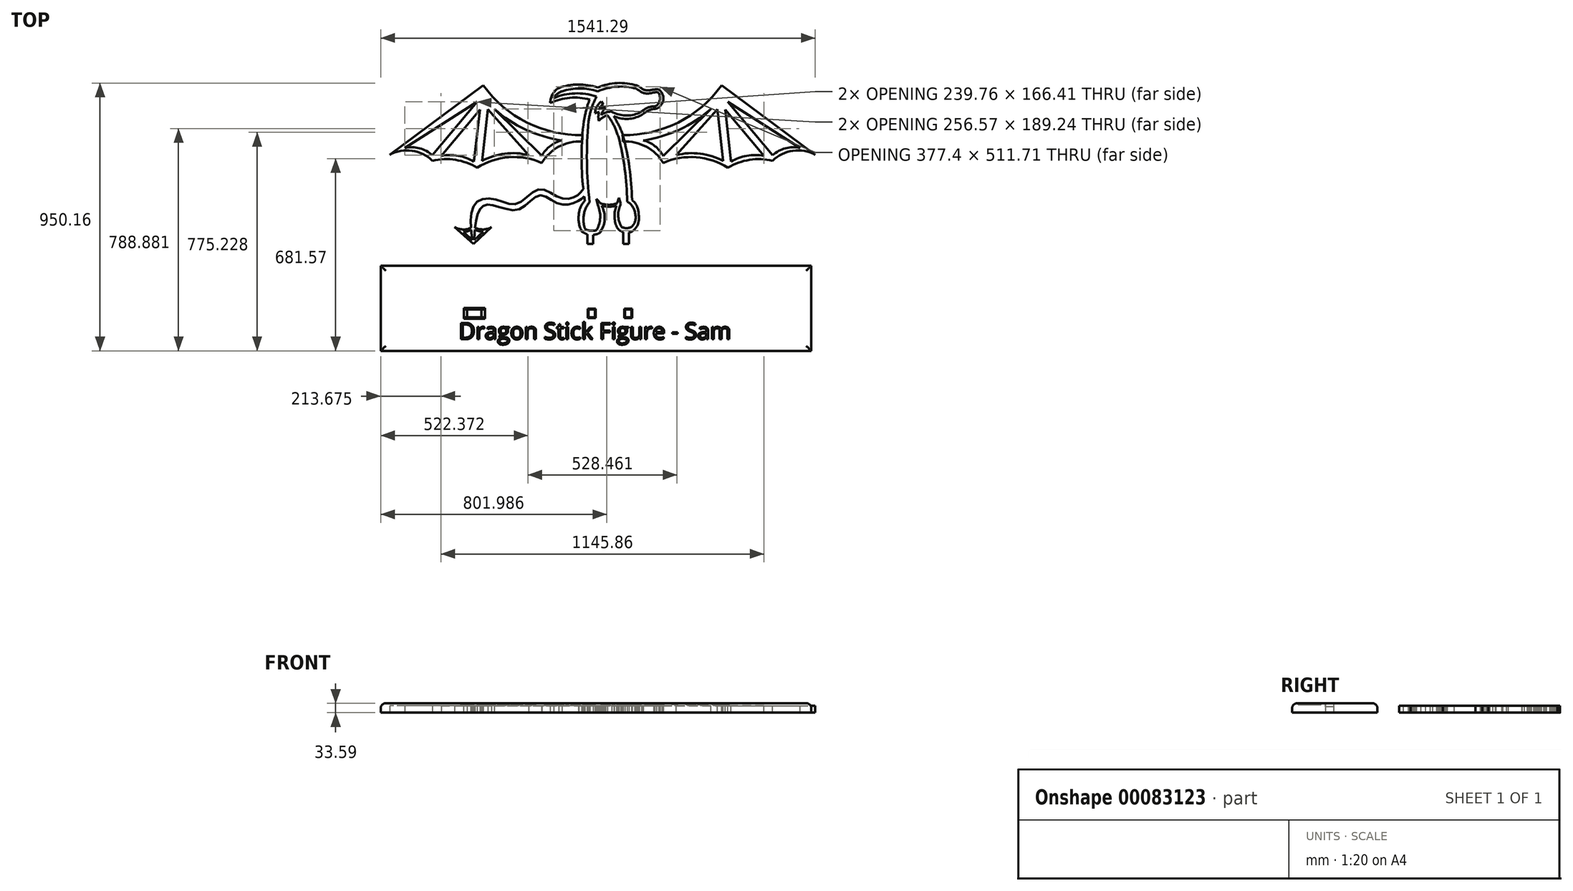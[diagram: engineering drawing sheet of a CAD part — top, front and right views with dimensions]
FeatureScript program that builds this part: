
annotation { "Feature Type Name" : "Feature", "Feature Type Description" : "" }
export const myFeature = defineFeature(function(context is Context, id is Id, definition is map)
    precondition{}
    {
        {
            var Q0;
            Q0=qCreatedBy(makeId("Top.planeOp"),FACE);
            var sketch = newSketch(context, id + "F0", { "sketchPlane" : qUnion([Q0])});
            skArc(sketch, "E0", {"start": v(-484.43, 280.49) * mm, "mid": v(-553.48, 287.44) * mm, "end": v(-620.94, 271.12) * mm});
            skFitSpline(sketch, "E1", {"points": [v(-484.43, 280.49) * mm, v(-460.99, 265.97) * mm, v(-442.45, 263.54) * mm, v(-427.16, 265.56) * mm, v(-405.15, 265.8) * mm], "startDerivative": vector(138.37, -75.5) * mm, "endDerivative": vector(39.99, -52.16) * mm});
            skArc(sketch, "E2", {"start": v(-412.1, 219.74) * mm, "mid": v(-400.2, 241.5) * mm, "end": v(-405.15, 265.8) * mm});
            skArc(sketch, "E3", {"start": v(-422.32, 217.88) * mm, "mid": v(-445.34, 212.23) * mm, "end": v(-465.2, 199.3) * mm});
            skFitSpline(sketch, "E4", {"points": [v(-422.32, 217.88) * mm, v(-417.9, 217.88) * mm, v(-412.1, 219.74) * mm], "startDerivative": vector(9.34, -0.8) * mm, "endDerivative": vector(11.04, 4.36) * mm});
            skArc(sketch, "E5", {"start": v(-571.52, 199) * mm, "mid": v(-522.88, 185.43) * mm, "end": v(-473.31, 195.06) * mm});
            skFitSpline(sketch, "E6", {"points": [v(-473.31, 195.06) * mm, v(-468.57, 197.4) * mm, v(-465.2, 199.3) * mm], "startDerivative": vector(9.2, 4.4) * mm, "endDerivative": vector(6.96, 4.05) * mm});
            skArc(sketch, "E7", {"start": v(-620.94, 271.12) * mm, "mid": v(-684.3, 280.9) * mm, "end": v(-747.67, 271.1) * mm});
            skArc(sketch, "E8", {"start": v(-621.17, 284.55) * mm, "mid": v(-690.53, 295.4) * mm, "end": v(-759.58, 282.78) * mm});
            skArc(sketch, "E9", {"start": v(-481.37, 291.76) * mm, "mid": v(-551.9, 300.36) * mm, "end": v(-621.17, 284.55) * mm});
            skFitSpline(sketch, "E10", {"points": [v(-481.37, 291.76) * mm, v(-459.76, 277.82) * mm, v(-442.69, 274.68) * mm, v(-425.28, 276.74) * mm, v(-404.78, 277.02) * mm], "startDerivative": vector(140.51, -71.44) * mm, "endDerivative": vector(88.36, -26.77) * mm});
            skArc(sketch, "E11", {"start": v(-399.61, 218.82) * mm, "mid": v(-388.09, 240.85) * mm, "end": v(-393.55, 265.1) * mm});
            skFitSpline(sketch, "E12", {"points": [v(-404.78, 277.02) * mm, v(-400.06, 273.87) * mm, v(-395.78, 269.14) * mm, v(-393.55, 265.1) * mm], "startDerivative": vector(12.2, -10.5) * mm, "endDerivative": vector(5.8, -13.5) * mm});
            skArc(sketch, "E13", {"start": v(-418.36, 208.78) * mm, "mid": v(-440.62, 203.04) * mm, "end": v(-459.86, 190.48) * mm});
            skFitSpline(sketch, "E14", {"points": [v(-418.36, 208.78) * mm, v(-413.9, 209.67) * mm, v(-409.93, 210.81) * mm, v(-405.82, 212.87) * mm, v(-402.08, 215.77) * mm, v(-399.61, 218.82) * mm], "startDerivative": vector(19.06, 3.38) * mm, "endDerivative": vector(13.35, 14.43) * mm});
            skArc(sketch, "E15", {"start": v(-571.39, 187.02) * mm, "mid": v(-522.75, 173.44) * mm, "end": v(-473.18, 183.07) * mm});
            skFitSpline(sketch, "E16", {"points": [v(-473.18, 183.07) * mm, v(-468.57, 185.12) * mm, v(-464.55, 187.8) * mm, v(-459.86, 190.48) * mm], "startDerivative": vector(12.57, 6.02) * mm, "endDerivative": vector(11.63, 6.29) * mm});
            skArc(sketch, "E17", {"start": v(-571.52, 199) * mm, "mid": v(-590.86, 196.58) * mm, "end": v(-608, 187.3) * mm});
            skArc(sketch, "E18", {"start": v(-592.56, 213.03) * mm, "mid": v(-602.14, 201.29) * mm, "end": v(-608, 187.3) * mm});
            skArc(sketch, "E19", {"start": v(-592.56, 213.03) * mm, "mid": v(-604.54, 212.08) * mm, "end": v(-616, 208.46) * mm});
            skArc(sketch, "E20", {"start": v(-601.14, 225.6) * mm, "mid": v(-609.5, 217.84) * mm, "end": v(-616, 208.46) * mm});
            skArc(sketch, "E21", {"start": v(-571.39, 187.02) * mm, "mid": v(-596.73, 182.14) * mm, "end": v(-616.75, 165.84) * mm});
            skArc(sketch, "E22", {"start": v(-616, 197.02) * mm, "mid": v(-618.73, 181.49) * mm, "end": v(-616.75, 165.84) * mm});
            skArc(sketch, "E23", {"start": v(-616, 197.02) * mm, "mid": v(-623.27, 195.8) * mm, "end": v(-630.3, 193.6) * mm});
            skArc(sketch, "E24", {"start": v(-608, 234.75) * mm, "mid": v(-623.95, 216.78) * mm, "end": v(-630.3, 193.6) * mm});
            skLineSegment(sketch, "E25", {"start": v(-608, 234.75) * mm, "end": v(-601.14, 225.6) * mm});
            skArc(sketch, "E26", {"start": v(-747.67, 271.1) * mm, "mid": v(-764.57, 261.68) * mm, "end": v(-777.2, 247.01) * mm});
            skArc(sketch, "E27", {"start": v(-626.3, 252.48) * mm, "mid": v(-702.26, 263.77) * mm, "end": v(-777.2, 247.01) * mm});
            skArc(sketch, "E28", {"start": v(-648.73, 242.02) * mm, "mid": v(-720.12, 248.02) * mm, "end": v(-789.38, 229.68) * mm});
            skArc(sketch, "E29", {"start": v(-759.58, 282.78) * mm, "mid": v(-781.46, 260.15) * mm, "end": v(-789.38, 229.68) * mm});
            skFitSpline(sketch, "E30", {"points": [v(-626.3, 252.48) * mm, v(-637.17, 226.96) * mm, v(-647.34, 194.9) * mm, v(-653.4, 165.01) * mm], "startDerivative": vector(-23.44, -90.04) * mm, "endDerivative": vector(-15.76, -95.9) * mm});
            skArc(sketch, "E31", {"start": v(-669.93, 166.15) * mm, "mid": v(-678.05, 24.8) * mm, "end": v(-666.54, -116.32) * mm});
            skFitSpline(sketch, "E32", {"points": [v(-669.93, 166.15) * mm, v(-664.3, 192.64) * mm, v(-654.82, 227.81) * mm, v(-648.73, 242.02) * mm], "startDerivative": vector(12.93, 74.9) * mm, "endDerivative": vector(30.43, 52.72) * mm});
            skArc(sketch, "E33", {"start": v(-653.4, 165.01) * mm, "mid": v(-659.24, 21.16) * mm, "end": v(-649.6, -122.5) * mm});
            skArc(sketch, "E34", {"start": v(-670.97, -177.12) * mm, "mid": v(-670.63, -196.15) * mm, "end": v(-666.82, -214.8) * mm});
            skArc(sketch, "E35", {"start": v(-687.44, -160.73) * mm, "mid": v(-687.67, -194.27) * mm, "end": v(-677.18, -226.13) * mm});
            skArc(sketch, "E36", {"start": v(-624.6, -220.87) * mm, "mid": v(-612.15, -177.08) * mm, "end": v(-620.85, -132.38) * mm});
            skArc(sketch, "E37", {"start": v(-677.18, -226.13) * mm, "mid": v(-646.07, -238.08) * mm, "end": v(-613.5, -231.05) * mm});
            skArc(sketch, "E38", {"start": v(-613.5, -231.05) * mm, "mid": v(-596.6, -168.62) * mm, "end": v(-625.32, -110.68) * mm});
            skArc(sketch, "E39", {"start": v(-666.54, -116.32) * mm, "mid": v(-680.3, -136.97) * mm, "end": v(-687.44, -160.73) * mm});
            skArc(sketch, "E40", {"start": v(-649.6, -122.5) * mm, "mid": v(-665.2, -147.88) * mm, "end": v(-670.97, -177.12) * mm});
            skLineSegment(sketch, "E41", {"start": v(-625.32, -110.68) * mm, "end": v(-620.85, -132.38) * mm});
            skFitSpline(sketch, "E42", {"points": [v(-666.82, -214.8) * mm, v(-660.47, -219.86) * mm, v(-651.59, -222.63) * mm, v(-639.03, -223.86) * mm, v(-624.6, -220.87) * mm], "startDerivative": vector(25.62, -29.25) * mm, "endDerivative": vector(37, 23.92) * mm});
            skArc(sketch, "E43", {"start": v(-606.94, -134.54) * mm, "mid": v(-580.81, -138.28) * mm, "end": v(-554.8, -133.74) * mm});
            skArc(sketch, "E44", {"start": v(-612.77, -125.06) * mm, "mid": v(-582.71, -131.29) * mm, "end": v(-552.42, -126.32) * mm});
            skLineSegment(sketch, "E45", {"start": v(-656.93, -236.2) * mm, "end": v(-656.93, -269.78) * mm});
            skLineSegment(sketch, "E46", {"start": v(-656.93, -269.78) * mm, "end": v(-636.93, -269.78) * mm});
            skLineSegment(sketch, "E47", {"start": v(-636.93, -269.78) * mm, "end": v(-636.93, -238.07) * mm});
            skFitSpline(sketch, "E48", {"points": [v(-563.7, 183.16) * mm, v(-555, 167.43) * mm, v(-543.29, 145.13) * mm, v(-531.58, 114.44) * mm], "startDerivative": vector(37.97, -52.48) * mm, "endDerivative": vector(15.54, -59.33) * mm});
            skArc(sketch, "E49", {"start": v(-499.3, -114.58) * mm, "mid": v(-508.47, 0.91) * mm, "end": v(-531.58, 114.44) * mm});
            skArc(sketch, "E50", {"start": v(-516.28, -120.2) * mm, "mid": v(-524.75, -4.53) * mm, "end": v(-547.2, 109.26) * mm});
            skFitSpline(sketch, "E51", {"points": [v(-547.2, 109.26) * mm, v(-554.8, 129.44) * mm, v(-560.43, 143.95) * mm, v(-567.6, 157.47) * mm, v(-578.06, 175.21) * mm, v(-585.94, 185.82) * mm], "startDerivative": vector(-35.46, 93.18) * mm, "endDerivative": vector(-43.63, 54.6) * mm});
            skArc(sketch, "E52", {"start": v(-500.28, -209.14) * mm, "mid": v(-494.03, -201.9) * mm, "end": v(-489.57, -193.45) * mm});
            skArc(sketch, "E53", {"start": v(-537.04, -209.14) * mm, "mid": v(-518.66, -214.33) * mm, "end": v(-500.28, -209.14) * mm});
            skArc(sketch, "E54", {"start": v(-538.85, -128.02) * mm, "mid": v(-548.16, -168.8) * mm, "end": v(-537.04, -209.14) * mm});
            skFitSpline(sketch, "E55", {"points": [v(-499.3, -114.58) * mm, v(-483.88, -131.79) * mm, v(-474.9, -168.24) * mm, v(-478.48, -200.18) * mm, v(-500.9, -226.64) * mm, v(-532.8, -226.94) * mm, v(-552.6, -210.97) * mm, v(-560.81, -175.52) * mm, v(-557.63, -143.7) * mm, v(-545.72, -106.52) * mm], "startDerivative": vector(166.99, -141.57) * mm, "endDerivative": vector(81.99, 252.34) * mm});
            skLineSegment(sketch, "E56", {"start": v(-538.85, -128.02) * mm, "end": v(-545.72, -106.52) * mm});
            skFitSpline(sketch, "E57", {"points": [v(-489.57, -193.45) * mm, v(-486.38, -179.96) * mm, v(-488.47, -159.37) * mm, v(-493.52, -144.09) * mm, v(-503.77, -129.23) * mm, v(-516.28, -120.2) * mm], "startDerivative": vector(23.3, 68.6) * mm, "endDerivative": vector(-67.73, 40.79) * mm});
            skLineSegment(sketch, "E58", {"start": v(-529.91, -269.78) * mm, "end": v(-529.91, -227.85) * mm});
            skLineSegment(sketch, "E59", {"start": v(-529.91, -269.78) * mm, "end": v(-509.91, -269.78) * mm});
            skLineSegment(sketch, "E60", {"start": v(-509.91, -269.78) * mm, "end": v(-509.91, -229.32) * mm});
            skArc(sketch, "E61", {"start": v(-1026.56, 291.98) * mm, "mid": v(-872.42, 160.84) * mm, "end": v(-675.07, 115.98) * mm});
            skLineSegment(sketch, "E62", {"start": v(-1026.56, 291.98) * mm, "end": v(-1358.57, 46.23) * mm});
            skArc(sketch, "E63", {"start": v(-1026.56, 247.98) * mm, "mid": v(-868.74, 131.69) * mm, "end": v(-676.61, 92.69) * mm});
            skLineSegment(sketch, "E64", {"start": v(-1034.74, 243.13) * mm, "end": v(-1059.42, 21.63) * mm});
            skLineSegment(sketch, "E65", {"start": v(-1021.73, 242.53) * mm, "end": v(-1048.75, 0) * mm});
            skLineSegment(sketch, "E66", {"start": v(-1010.63, 230.68) * mm, "end": v(-819.5, 17.2) * mm});
            skLineSegment(sketch, "E67", {"start": v(-1036.4, 228.13) * mm, "end": v(-1206.74, 24.83) * mm});
            skLineSegment(sketch, "E68", {"start": v(-1044.26, 239.06) * mm, "end": v(-1207.08, 44.73) * mm});
            skArc(sketch, "E69", {"start": v(-1206.74, 24.83) * mm, "mid": v(-1279.2, 60.02) * mm, "end": v(-1358.57, 46.23) * mm});
            skArc(sketch, "E70", {"start": v(-1207.08, 44.73) * mm, "mid": v(-1253.13, 68.87) * mm, "end": v(-1305.1, 70.33) * mm});
            skLineSegment(sketch, "E71", {"start": v(-1026.56, 247.98) * mm, "end": v(-1305.1, 70.33) * mm});
            skArc(sketch, "E72", {"start": v(-1048.75, 0) * mm, "mid": v(-1125.3, 27.95) * mm, "end": v(-1206.74, 24.83) * mm});
            skArc(sketch, "E73", {"start": v(-1059.42, 21.63) * mm, "mid": v(-1115.87, 42.63) * mm, "end": v(-1176.1, 42.6) * mm});
            skLineSegment(sketch, "E74", {"start": v(-1176.1, 42.6) * mm, "end": v(-1038.82, 206.46) * mm});
            skArc(sketch, "E75", {"start": v(-819.5, 17.2) * mm, "mid": v(-936.27, 37.18) * mm, "end": v(-1048.75, 0) * mm});
            skArc(sketch, "E76", {"start": v(-865.75, 44.87) * mm, "mid": v(-950.54, 50) * mm, "end": v(-1031.44, 24.12) * mm});
            skLineSegment(sketch, "E77", {"start": v(-1031.44, 24.12) * mm, "end": v(-1008.67, 228.5) * mm});
            skLineSegment(sketch, "E78", {"start": v(-865.75, 44.87) * mm, "end": v(-1011.05, 207.16) * mm});
            skArc(sketch, "E79", {"start": v(-676.61, 92.69) * mm, "mid": v(-758.5, 74.7) * mm, "end": v(-819.5, 17.2) * mm});
            skLineSegment(sketch, "E80", {"start": v(-988, 208.9) * mm, "end": v(-819.18, 42.5) * mm});
            skArc(sketch, "E81", {"start": v(-748.24, 97.13) * mm, "mid": v(-789.3, 77.08) * mm, "end": v(-819.18, 42.5) * mm});
            skFitSpline(sketch, "E82", {"points": [v(-671.96, -75.01) * mm, v(-697.53, -101.03) * mm, v(-752.8, -107.27) * mm, v(-829.54, -76.64) * mm, v(-908.1, -127.93) * mm, v(-993.52, -109.8) * mm, v(-1058.82, -132.11) * mm, v(-1069.13, -226.43) * mm, v(-1061.71, -269.78) * mm], "startDerivative": vector(-219.44, -364.8) * mm, "endDerivative": vector(110.19, -346.24) * mm});
            skFitSpline(sketch, "E83", {"points": [v(-668.7, -101.41) * mm, v(-697.53, -121.57) * mm, v(-759.3, -128.05) * mm, v(-828.36, -98.23) * mm, v(-899.38, -147.58) * mm, v(-994.97, -132.34) * mm, v(-1036.5, -144.45) * mm, v(-1056.73, -223.82) * mm, v(-1061.71, -269.78) * mm], "startDerivative": vector(-137.18, -225.27) * mm, "endDerivative": vector(-97.33, -397) * mm});
            skLineSegment(sketch, "E84", {"start": v(-1061.71, -269.78) * mm, "end": v(-997.33, -210.46) * mm});
            skLineSegment(sketch, "E85", {"start": v(-1061.71, -269.78) * mm, "end": v(-1128.04, -210.46) * mm});
            skLineSegment(sketch, "E86", {"start": v(-1096.5, -227.71) * mm, "end": v(-1065.28, -255.64) * mm});
            skLineSegment(sketch, "E87", {"start": v(-1027.33, -226.55) * mm, "end": v(-1059.26, -255.97) * mm});
            skArc(sketch, "E88", {"start": v(-1128.04, -210.46) * mm, "mid": v(-1099.45, -219.05) * mm, "end": v(-1070.27, -212.75) * mm});
            skArc(sketch, "E89", {"start": v(-1055.67, -212.75) * mm, "mid": v(-1026.21, -218.92) * mm, "end": v(-997.33, -210.46) * mm});
            skArc(sketch, "E90", {"start": v(-1096.5, -227.71) * mm, "mid": v(-1082.64, -225.42) * mm, "end": v(-1069.72, -219.91) * mm});
            skArc(sketch, "E91", {"start": v(-1056.39, -219.91) * mm, "mid": v(-1042.22, -224.82) * mm, "end": v(-1027.33, -226.55) * mm});
            skLineSegment(sketch, "E92.bottom", {"start": v(-653.73, -531) * mm, "end": v(-630.87, -531) * mm});
            skLineSegment(sketch, "E92.top", {"start": v(-653.73, -502.38) * mm, "end": v(-630.87, -502.38) * mm});
            skLineSegment(sketch, "E92.left", {"start": v(-653.73, -531) * mm, "end": v(-653.73, -502.38) * mm});
            skLineSegment(sketch, "E92.right", {"start": v(-630.87, -531) * mm, "end": v(-630.87, -502.38) * mm});
            skLineSegment(sketch, "E93.bottom", {"start": v(-523.85, -531) * mm, "end": v(-500.99, -531) * mm});
            skLineSegment(sketch, "E93.top", {"start": v(-523.85, -502.38) * mm, "end": v(-500.99, -502.38) * mm});
            skLineSegment(sketch, "E93.left", {"start": v(-523.85, -531) * mm, "end": v(-523.85, -502.38) * mm});
            skLineSegment(sketch, "E93.right", {"start": v(-500.99, -531) * mm, "end": v(-500.99, -502.38) * mm});
            skLineSegment(sketch, "E94.bottom", {"start": v(-1033.1, -531) * mm, "end": v(-1083.9, -531) * mm});
            skLineSegment(sketch, "E94.top", {"start": v(-1033.1, -502.43) * mm, "end": v(-1083.9, -502.43) * mm});
            skLineSegment(sketch, "E94.left", {"start": v(-1033.1, -531) * mm, "end": v(-1033.1, -502.43) * mm});
            skLineSegment(sketch, "E94.right", {"start": v(-1083.9, -531) * mm, "end": v(-1083.9, -502.43) * mm});
            skLineSegment(sketch, "E95.bottom", {"start": v(-1390.5, -347.16) * mm, "end": v(136.52, -347.16) * mm});
            skLineSegment(sketch, "E95.top", {"start": v(-1390.5, -649.53) * mm, "end": v(136.52, -649.53) * mm});
            skLineSegment(sketch, "E95.left", {"start": v(-1390.5, -347.16) * mm, "end": v(-1390.5, -649.53) * mm});
            skLineSegment(sketch, "E95.right", {"start": v(136.52, -347.16) * mm, "end": v(136.52, -649.53) * mm});
            skPoint(sketch, "E96", {"position": v(-1058.5, -516.72) * mm});
            skPoint(sketch, "E96.positionSnap0", {"position": v(-1033.1, -516.72) * mm});
            skPoint(sketch, "E96.positionSnap1", {"position": v(-1058.5, -502.43) * mm});
            skSolve(sketch);
        }
        {
            var Q0;
            Q0=makeQuery(id+"F0.imprint","IMPRINT",FACE,{"disambiguationData":[TD([[makeQuery(id+"F0.imprint","IMPRINT",EDGE,{"derivedFrom":sQuery(id+"F0.wireOp",EDGE,"E92.bottom")}),-1.0]])]});
            extrude(context, id + "F1", {"entities" : qUnion([Q0]), "depth" : 33.6 * mm});
        }
        {
            var Q0;
            {var subQ13=sQuery(id+"F0.wireOp",EDGE,"E61");Q0=makeQuery(id+"F0.imprint","IMPRINT",FACE,{"disambiguationData":[TD([[makeQuery(id+"F0.imprint","IMPRINT",EDGE,{"derivedFrom":subQ13}),-1.0]])]});}
            var Q1;
            {var subQ4=sQuery(id+"F0.wireOp",EDGE,"E80");Q1=makeQuery(id+"F0.imprint","IMPRINT",FACE,{"disambiguationData":[TD([[makeQuery(id+"F0.imprint","IMPRINT",EDGE,{"derivedFrom":subQ4}),-1.0]])]});}
            var Q2;
            {var subQ6=sQuery(id+"F0.wireOp",EDGE,"E65");Q2=makeQuery(id+"F0.imprint","IMPRINT",FACE,{"disambiguationData":[TD([[makeQuery(id+"F0.imprint","IMPRINT",EDGE,{"derivedFrom":subQ6}),1.0]])]});}
            var Q3;
            {var subQ0=sQuery(id+"F0.wireOp",EDGE,"E65");Q3=makeQuery(id+"F0.imprint","IMPRINT",FACE,{"disambiguationData":[TD([[makeQuery(id+"F0.imprint","IMPRINT",EDGE,{"derivedFrom":subQ0}),-1.0]])]});}
            extrude(context, id + "F2", {"entities" : qUnion([Q0, Q1, Q2, Q3]), "depth" : 25 * mm});
        }
        {
            var Q0;
            Q0=makeQuery(id+"F2.opExtrude","SWEPT_BODY",BODY,{"disambiguationData":[OSD([sQuery(id+"F0.wireOp",EDGE,"E31"),sQuery(id+"F0.wireOp",EDGE,"E61"),sQuery(id+"F0.wireOp",EDGE,"E62"),sQuery(id+"F0.wireOp",EDGE,"E63"),sQuery(id+"F0.wireOp",EDGE,"E64"),sQuery(id+"F0.wireOp",EDGE,"E68"),sQuery(id+"F0.wireOp",EDGE,"E69"),sQuery(id+"F0.wireOp",EDGE,"E70"),sQuery(id+"F0.wireOp",EDGE,"E71"),sQuery(id+"F0.wireOp",EDGE,"E72"),sQuery(id+"F0.wireOp",EDGE,"E73"),sQuery(id+"F0.wireOp",EDGE,"E74"),sQuery(id+"F0.wireOp",EDGE,"E75"),sQuery(id+"F0.wireOp",EDGE,"E76"),sQuery(id+"F0.wireOp",EDGE,"E77"),sQuery(id+"F0.wireOp",EDGE,"E78"),sQuery(id+"F0.wireOp",EDGE,"E79"),sQuery(id+"F0.wireOp",EDGE,"E80"),sQuery(id+"F0.wireOp",EDGE,"E81")])]});
            var Q1;
            Q1=sQuery(id+"F0.wireOp",EDGE,"E92.right");
            transform(context, id + "F3", {"entities" : qUnion([Q0]), "transformType" : TransformType.ROTATION, "transformAxis" : qUnion([Q1]), "angle" : 180 * degree, "makeCopy" : true});
        }
        {
            var Q0;
            Q0=makeQuery(id+"F3.opPattern","COPY",BODY,{"derivedFrom":makeQuery(id+"F2.opExtrude","SWEPT_BODY",BODY,{"disambiguationData":[OSD([sQuery(id+"F0.wireOp",EDGE,"E31"),sQuery(id+"F0.wireOp",EDGE,"E61"),sQuery(id+"F0.wireOp",EDGE,"E62"),sQuery(id+"F0.wireOp",EDGE,"E63"),sQuery(id+"F0.wireOp",EDGE,"E64"),sQuery(id+"F0.wireOp",EDGE,"E68"),sQuery(id+"F0.wireOp",EDGE,"E69"),sQuery(id+"F0.wireOp",EDGE,"E70"),sQuery(id+"F0.wireOp",EDGE,"E71"),sQuery(id+"F0.wireOp",EDGE,"E72"),sQuery(id+"F0.wireOp",EDGE,"E73"),sQuery(id+"F0.wireOp",EDGE,"E74"),sQuery(id+"F0.wireOp",EDGE,"E75"),sQuery(id+"F0.wireOp",EDGE,"E76"),sQuery(id+"F0.wireOp",EDGE,"E77"),sQuery(id+"F0.wireOp",EDGE,"E78"),sQuery(id+"F0.wireOp",EDGE,"E79"),sQuery(id+"F0.wireOp",EDGE,"E80"),sQuery(id+"F0.wireOp",EDGE,"E81")])]}),"instanceName":"1"});
            transform(context, id + "F4", {"entities" : qUnion([Q0]), "transformType" : TransformType.TRANSLATION_3D, "dx" : 60 * mm, "dy" : 0 * mm, "dz" : 25 * mm, "makeCopy" : false});
        }
        {
            var Q0;
            {var subQ0=sQuery(id+"F0.wireOp",EDGE,"E82");var subQ7=sQuery(id+"F0.wireOp",EDGE,"E31");var subQ8=makeQuery(id+"F0.imprint","INTERSECT",VERTEX,{"derivedFrom":[subQ7,subQ0]});Q0=makeQuery(id+"F0.imprint","IMPRINT",FACE,{"disambiguationData":[TD([[makeQuery(id+"F0.imprint","IMPRINT",EDGE,{"disambiguationData":[TD([[subQ8,-1.0]])],"derivedFrom":subQ7}),-1.0]])]});}
            var Q1;
            {var subQ1=sQuery(id+"F0.wireOp",EDGE,"E84");Q1=makeQuery(id+"F0.imprint","IMPRINT",FACE,{"disambiguationData":[TD([[makeQuery(id+"F0.imprint","IMPRINT",EDGE,{"derivedFrom":subQ1}),1.0]])]});}
            var Q2;
            {var subQ1=sQuery(id+"F0.wireOp",EDGE,"E85");Q2=makeQuery(id+"F0.imprint","IMPRINT",FACE,{"disambiguationData":[TD([[makeQuery(id+"F0.imprint","IMPRINT",EDGE,{"derivedFrom":subQ1}),-1.0]])]});}
            var Q3;
            Q3=makeQuery(id+"F0.imprint","IMPRINT",FACE,{"disambiguationData":[TD([[makeQuery(id+"F0.imprint","IMPRINT",EDGE,{"derivedFrom":sQuery(id+"F0.wireOp",EDGE,"E0")}),-1.0]])]});
            var Q4;
            {var subQ0=sQuery(id+"F0.wireOp",EDGE,"E45");Q4=makeQuery(id+"F0.imprint","IMPRINT",FACE,{"disambiguationData":[TD([[makeQuery(id+"F0.imprint","IMPRINT",EDGE,{"derivedFrom":subQ0}),1.0]])]});}
            var Q5;
            {var subQ0=sQuery(id+"F0.wireOp",EDGE,"E58");Q5=makeQuery(id+"F0.imprint","IMPRINT",FACE,{"disambiguationData":[TD([[makeQuery(id+"F0.imprint","IMPRINT",EDGE,{"derivedFrom":subQ0}),-1.0]])]});}
            var Q6;
            {var subQ3=sQuery(id+"F0.wireOp",EDGE,"E48");Q6=makeQuery(id+"F0.imprint","IMPRINT",FACE,{"disambiguationData":[TD([[makeQuery(id+"F0.imprint","IMPRINT",EDGE,{"derivedFrom":subQ3}),-1.0]])]});}
            var Q7;
            {var subQ0=sQuery(id+"F0.wireOp",EDGE,"E43");Q7=makeQuery(id+"F0.imprint","IMPRINT",FACE,{"disambiguationData":[TD([[makeQuery(id+"F0.imprint","IMPRINT",EDGE,{"derivedFrom":subQ0}),1.0]])]});}
            extrude(context, id + "F5", {"entities" : qUnion([Q0, Q1, Q2, Q3, Q4, Q5, Q6, Q7]), "depth" : 25 * mm});
        }
        {
            var Q0;
            Q0=makeQuery(id+"F1.opExtrude","CAP_EDGE",EDGE,{"disambiguationData":[OSD([sQuery(id+"F0.wireOp",EDGE,"E94.left")])],"isStart":false});
            var Q1;
            Q1=makeQuery(id+"F1.opExtrude","CAP_EDGE",EDGE,{"disambiguationData":[OSD([sQuery(id+"F0.wireOp",EDGE,"E94.right")])],"isStart":false});
            chamfer(context, id + "F6", {"entities" : qUnion([Q0, Q1]), "width" : 12.14 * mm, "tangentPropagation" : true});
        }
        {
            var Q0;
            Q0=makeQuery(id+"F1.opExtrude","CAP_EDGE",EDGE,{"disambiguationData":[OSD([sQuery(id+"F0.wireOp",EDGE,"E94.top")])],"isStart":false});
            var Q1;
            Q1=makeQuery(id+"F1.opExtrude","CAP_EDGE",EDGE,{"disambiguationData":[OSD([sQuery(id+"F0.wireOp",EDGE,"E94.bottom")])],"isStart":false});
            chamfer(context, id + "F7", {"entities" : qUnion([Q0, Q1]), "width" : 5.08 * mm, "tangentPropagation" : true});
        }
        {
            var Q0;
            Q0=makeQuery(id+"F1.opExtrude","CAP_EDGE",EDGE,{"disambiguationData":[OSD([sQuery(id+"F0.wireOp",EDGE,"E95.left")])],"isStart":false});
            var Q1;
            Q1=makeQuery(id+"F1.opExtrude","CAP_EDGE",EDGE,{"disambiguationData":[OSD([sQuery(id+"F0.wireOp",EDGE,"E95.top")])],"isStart":false});
            var Q2;
            Q2=makeQuery(id+"F1.opExtrude","CAP_EDGE",EDGE,{"disambiguationData":[OSD([sQuery(id+"F0.wireOp",EDGE,"E95.bottom")])],"isStart":false});
            var Q3;
            Q3=makeQuery(id+"F1.opExtrude","CAP_EDGE",EDGE,{"disambiguationData":[OSD([sQuery(id+"F0.wireOp",EDGE,"E95.right")])],"isStart":false});
            fillet(context, id + "F8", {"entities" : qUnion([Q0, Q1, Q2, Q3]), "radius" : 17.78 * mm, "tangentPropagation" : true, "allowEdgeOverflow" : false});
        }
        {
            var Q0;
            Q0=makeQuery(id+"F1.opExtrude","CAP_EDGE",EDGE,{"disambiguationData":[OSD([sQuery(id+"F0.wireOp",EDGE,"E92.top")])],"isStart":false});
            var Q1;
            Q1=makeQuery(id+"F1.opExtrude","CAP_EDGE",EDGE,{"disambiguationData":[OSD([sQuery(id+"F0.wireOp",EDGE,"E92.bottom")])],"isStart":false});
            var Q2;
            Q2=makeQuery(id+"F1.opExtrude","CAP_EDGE",EDGE,{"disambiguationData":[OSD([sQuery(id+"F0.wireOp",EDGE,"E92.left")])],"isStart":false});
            var Q3;
            Q3=makeQuery(id+"F1.opExtrude","CAP_EDGE",EDGE,{"disambiguationData":[OSD([sQuery(id+"F0.wireOp",EDGE,"E92.right")])],"isStart":false});
            var Q4;
            Q4=makeQuery(id+"F1.opExtrude","CAP_EDGE",EDGE,{"disambiguationData":[OSD([sQuery(id+"F0.wireOp",EDGE,"E93.left")])],"isStart":false});
            var Q5;
            Q5=makeQuery(id+"F1.opExtrude","CAP_EDGE",EDGE,{"disambiguationData":[OSD([sQuery(id+"F0.wireOp",EDGE,"E93.top")])],"isStart":false});
            var Q6;
            Q6=makeQuery(id+"F1.opExtrude","CAP_EDGE",EDGE,{"disambiguationData":[OSD([sQuery(id+"F0.wireOp",EDGE,"E93.bottom")])],"isStart":false});
            var Q7;
            Q7=makeQuery(id+"F1.opExtrude","CAP_EDGE",EDGE,{"disambiguationData":[OSD([sQuery(id+"F0.wireOp",EDGE,"E93.right")])],"isStart":false});
            chamfer(context, id + "F9", {"entities" : qUnion([Q0, Q1, Q2, Q3, Q4, Q5, Q6, Q7]), "width" : 2.54 * mm, "tangentPropagation" : true});
        }
        {
            var Q0;
            Q0=makeQuery(id+"F1.opExtrude","CAP_FACE",FACE,{"disambiguationData":[OSD([sQuery(id+"F0.wireOp",EDGE,"E92.bottom"),sQuery(id+"F0.wireOp",EDGE,"E92.top"),sQuery(id+"F0.wireOp",EDGE,"E92.left"),sQuery(id+"F0.wireOp",EDGE,"E92.right"),sQuery(id+"F0.wireOp",EDGE,"E93.bottom"),sQuery(id+"F0.wireOp",EDGE,"E93.top"),sQuery(id+"F0.wireOp",EDGE,"E93.left"),sQuery(id+"F0.wireOp",EDGE,"E93.right"),sQuery(id+"F0.wireOp",EDGE,"E94.bottom"),sQuery(id+"F0.wireOp",EDGE,"E94.top"),sQuery(id+"F0.wireOp",EDGE,"E94.left"),sQuery(id+"F0.wireOp",EDGE,"E94.right"),sQuery(id+"F0.wireOp",EDGE,"E95.bottom"),sQuery(id+"F0.wireOp",EDGE,"E95.top"),sQuery(id+"F0.wireOp",EDGE,"E95.left"),sQuery(id+"F0.wireOp",EDGE,"E95.right")])],"isStart":false});
            var sketch = newSketch(context, id + "F10", { "sketchPlane" : qUnion([Q0])});
            skText(sketch, "E97", { "text": "Dragon Stick Figure - Sam", "fontName": "OpenSans-Regular.ttf"});
            const initialGuessF10  = {"E97": [-1.11402, -0.60834, 1, 0, 0.05842]};
            skSetInitialGuess(sketch, initialGuessF10);
            skSolve(sketch);
        }
        {
            var Q0;
            Q0 = qSketchRegion(id + "F10", true);
            extrude(context, id + "F11", {"entities" : qUnion([Q0]), "operationType" : NewBodyOperationType.REMOVE, "oppositeDirection" : true, "depth" : 5.08 * mm});
        }
        {
            var Q0;
            Q0=makeQuery(id+"F3.opPattern","COPY",BODY,{"derivedFrom":makeQuery(id+"F2.opExtrude","SWEPT_BODY",BODY,{"disambiguationData":[OSD([sQuery(id+"F0.wireOp",EDGE,"E31"),sQuery(id+"F0.wireOp",EDGE,"E61"),sQuery(id+"F0.wireOp",EDGE,"E62"),sQuery(id+"F0.wireOp",EDGE,"E63"),sQuery(id+"F0.wireOp",EDGE,"E64"),sQuery(id+"F0.wireOp",EDGE,"E68"),sQuery(id+"F0.wireOp",EDGE,"E69"),sQuery(id+"F0.wireOp",EDGE,"E70"),sQuery(id+"F0.wireOp",EDGE,"E71"),sQuery(id+"F0.wireOp",EDGE,"E72"),sQuery(id+"F0.wireOp",EDGE,"E73"),sQuery(id+"F0.wireOp",EDGE,"E74"),sQuery(id+"F0.wireOp",EDGE,"E75"),sQuery(id+"F0.wireOp",EDGE,"E76"),sQuery(id+"F0.wireOp",EDGE,"E77"),sQuery(id+"F0.wireOp",EDGE,"E78"),sQuery(id+"F0.wireOp",EDGE,"E79"),sQuery(id+"F0.wireOp",EDGE,"E80"),sQuery(id+"F0.wireOp",EDGE,"E81")])]}),"instanceName":"1"});
            transform(context, id + "F12", {"entities" : qUnion([Q0]), "transformType" : TransformType.TRANSLATION_3D, "dx" : -6.03 * mm, "dy" : 0 * mm, "dz" : 0 * mm, "makeCopy" : false});
        }
    });
